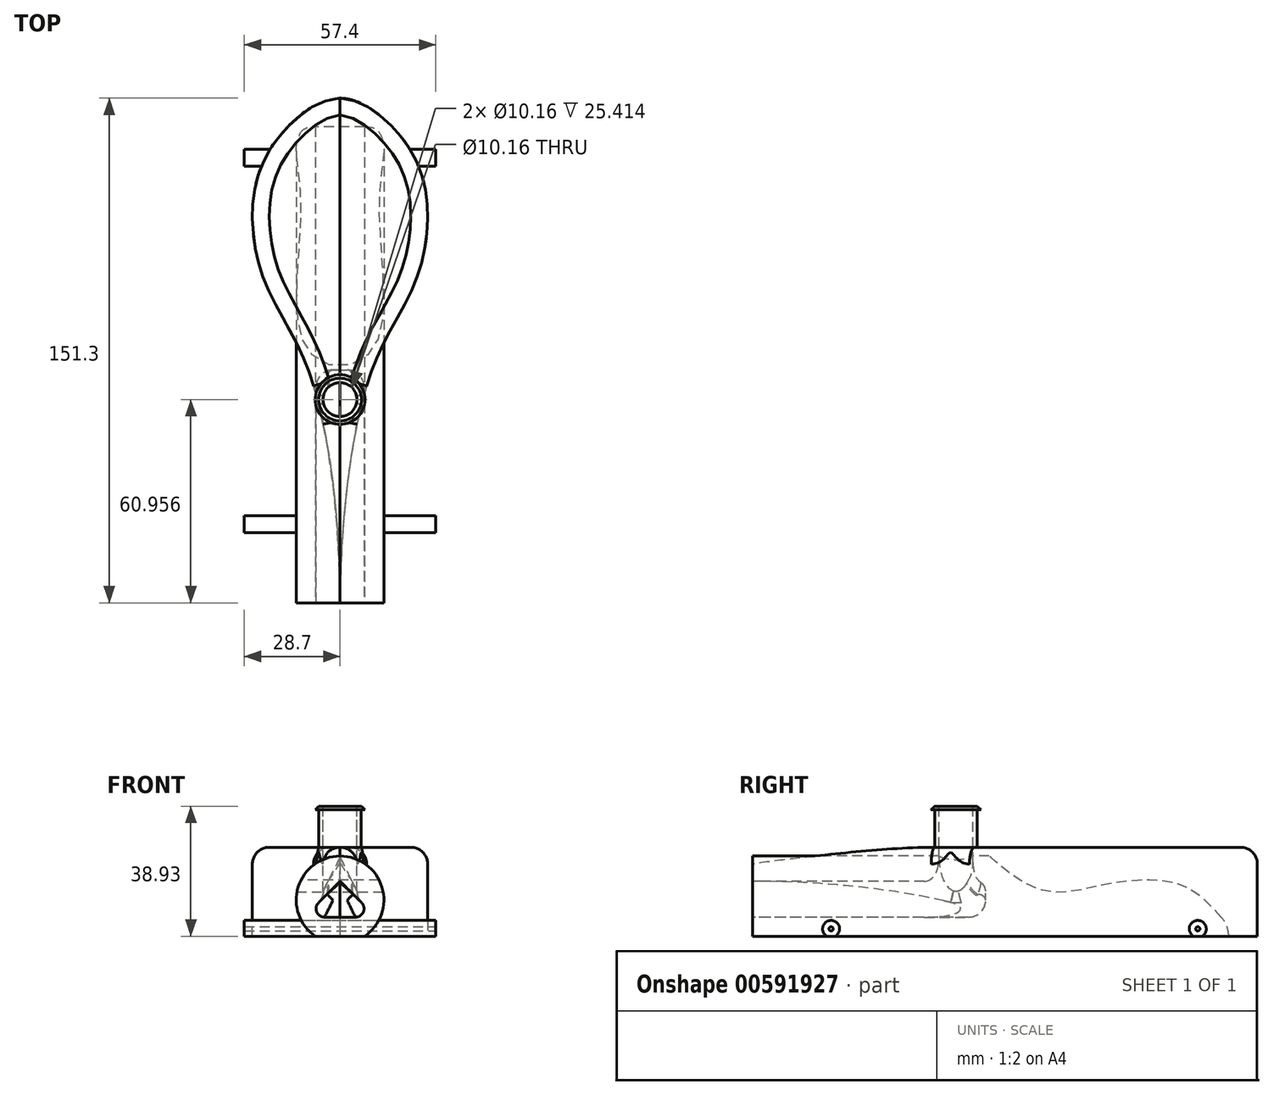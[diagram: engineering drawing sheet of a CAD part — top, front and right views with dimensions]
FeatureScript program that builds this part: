
annotation { "Feature Type Name" : "Feature", "Feature Type Description" : "" }
export const myFeature = defineFeature(function(context is Context, id is Id, definition is map)
    precondition{}
    {
        {
            var Q0;
            Q0=qCreatedBy(makeId("Right.planeOp"),FACE);
            var sketch = newSketch(context, id + "F0", { "sketchPlane" : qUnion([Q0])});
            skArc(sketch, "E0", {"start": v(34.57, 0) * mm, "mid": v(34, 3.03) * mm, "end": v(32.38, 5.66) * mm});
            skFitSpline(sketch, "E1", {"points": [v(32.38, 5.66) * mm, v(19.77, 15.55) * mm, v(-2.69, 15.42) * mm, v(-20.2, 13.5) * mm, v(-35.12, 22.16) * mm, v(-47.01, 29.03) * mm, v(-87.12, 25.6) * mm, v(-108.15, 26.13) * mm], "startDerivative": vector(-87.5, 96.16) * mm, "endDerivative": vector(-171.6, 17.01) * mm});
            skLineSegment(sketch, "E2", {"start": v(-108.15, 26.13) * mm, "end": v(-108.15, 0) * mm});
            skLineSegment(sketch, "E3", {"start": v(-108.15, 0) * mm, "end": v(34.57, 0) * mm});
            skSolve(sketch);
        }
        {
            var Q0;
            Q0=qSketchRegion(id+"F0",true);
            extrude(context, id + "F1", {"entities" : qUnion([Q0]), "endBound" : BoundingType.SYMMETRIC, "depth" : 50.8 * mm, "offsetDistance" : 25.4 * mm});
        }
        {
            var Q0;
            Q0=makeQuery(id+"F1.opExtrude","SWEPT_FACE",FACE,{"disambiguationData":[OSD([sQuery(id+"F0.wireOp",EDGE,"E2")])]});
            var sketch = newSketch(context, id + "F2", { "sketchPlane" : qUnion([Q0])});
            skCircle(sketch, "E4", {"center": v(0, 10.88) * mm, "radius": 13.14 * mm});
            skCircle(sketch, "E5", {"center": v(0, 10.88) * mm, "radius": 42.96 * mm});
            skSolve(sketch);
        }
        {
            var Q0;
            Q0 = qSketchRegion(id + "F2", true);
            extrude(context, id + "F3", {"entities" : qUnion([Q0]), "operationType" : NewBodyOperationType.REMOVE, "oppositeDirection" : true, "depth" : 175 * mm, "offsetDistance" : 25.4 * mm});
        }
        {
            var Q0;
            Q0=qCreatedBy(makeId("Top.planeOp"),FACE);
            var sketch = newSketch(context, id + "F4", { "sketchPlane" : qUnion([Q0])});
            skLineSegment(sketch, "E6", {"start": v(0, 43.15) * mm, "end": v(0, 43.15) * mm});
            skFitSpline(sketch, "E7", {"points": [v(0, 43.15) * mm, v(-11.67, 38.2) * mm, v(-24.8, 19.18) * mm, v(-22.86, -11.1) * mm, v(-9.97, -37.24) * mm, v(0, -108) * mm], "startDerivative": vector(-88.12, 0) * mm, "endDerivative": vector(1.08, -257.24) * mm});
            skLineSegment(sketch, "E8", {"start": v(0, -108) * mm, "end": v(0, 43.15) * mm});
            skSolve(sketch);
        }
        {
            var Q0;
            Q0 = qSketchRegion(id + "F4", true);
            extrude(context, id + "F5", {"entities" : qUnion([Q0]), "depth" : 26.67 * mm, "offsetDistance" : 25.4 * mm});
        }
        {
            var Q0;
            Q0=qCreatedBy(makeId("Right.planeOp"),FACE);
            var sketch = newSketch(context, id + "F6", { "sketchPlane" : qUnion([Q0])});
            skLineSegment(sketch, "E9", {"start": v(-47.2, 26.67) * mm, "end": v(-40.84, 26.67) * mm});
            skLineSegment(sketch, "E10", {"start": v(-40.84, 26.67) * mm, "end": v(-40.84, 37.94) * mm});
            skLineSegment(sketch, "E11", {"start": v(-40.84, 37.94) * mm, "end": v(-39.74, 37.94) * mm});
            skLineSegment(sketch, "E12", {"start": v(-39.74, 37.94) * mm, "end": v(-40.78, 38.93) * mm});
            skLineSegment(sketch, "E13", {"start": v(-40.78, 38.93) * mm, "end": v(-47.2, 38.93) * mm});
            skLineSegment(sketch, "E14", {"start": v(-47.2, 38.93) * mm, "end": v(-47.2, 26.67) * mm});
            skSolve(sketch);
        }
        {
            var Q0;
            Q0=qSketchRegion(id+"F6",true);
            var Q1;
            Q1=sQuery(id+"F6.wireOp",EDGE,"E14");
            revolve(context, id + "F7", {"operationType" : NewBodyOperationType.ADD, "entities" : qUnion([Q0]), "axis" : qUnion([Q1]), "revolveType" : RevolveType.FULL});
        }
        {
            var Q0;
            Q0=makeQuery(id+"F7.opRevolve","SWEPT_FACE",FACE,{"disambiguationData":[OSD([sQuery(id+"F6.wireOp",EDGE,"E13")])]});
            var sketch = newSketch(context, id + "F8", { "sketchPlane" : qUnion([Q0])});
            skCircle(sketch, "E15", {"center": v(0, -47.2) * mm, "radius": 5.08 * mm});
            skSolve(sketch);
        }
        {
            var Q0;
            Q0=qSketchRegion(id+"F8",true);
            extrude(context, id + "F9", {"entities" : qUnion([Q0]), "operationType" : NewBodyOperationType.REMOVE, "oppositeDirection" : true, "depth" : 32.77 * mm, "offsetDistance" : 25.4 * mm});
        }
        {
            var Q0;
            Q0=makeQuery(id+"F1.opExtrude","SWEPT_FACE",FACE,{"disambiguationData":[OSD([sQuery(id+"F0.wireOp",EDGE,"E2")])]});
            var sketch = newSketch(context, id + "F10", { "sketchPlane" : qUnion([Q0])});
            skLineSegment(sketch, "E16", {"start": v(0, 16.5) * mm, "end": v(-10.78, 5.71) * mm});
            skLineSegment(sketch, "E17", {"start": v(-10.78, 5.71) * mm, "end": v(0, 5.71) * mm});
            skLineSegment(sketch, "E18", {"start": v(0, 16.5) * mm, "end": v(10.78, 5.71) * mm});
            skLineSegment(sketch, "E19", {"start": v(10.78, 5.71) * mm, "end": v(0, 5.71) * mm});
            skSolve(sketch);
        }
        {
            var Q0;
            Q0=qSketchRegion(id+"F10",true);
            extrude(context, id + "F11", {"entities" : qUnion([Q0]), "operationType" : NewBodyOperationType.REMOVE, "endBound" : BoundingType.SYMMETRIC, "oppositeDirection" : true, "depth" : 139.7 * mm, "offsetDistance" : 25.4 * mm});
        }
        {
            var Q0;
            Q0=qCreatedBy(makeId("Right.planeOp"),FACE);
            var sketch = newSketch(context, id + "F12", { "sketchPlane" : qUnion([Q0])});
            skArc(sketch, "E20", {"start": v(-83.35, 0) * mm, "mid": v(-84.62, 4.74) * mm, "end": v(-85.89, 0) * mm});
            skCircle(sketch, "E21", {"center": v(-84.62, 2.2) * mm, "radius": 0.64 * mm});
            skLineSegment(sketch, "E22", {"start": v(-83.35, 0) * mm, "end": v(-85.89, 0) * mm});
            skArc(sketch, "E23", {"start": v(26.57, 0) * mm, "mid": v(25.3, 4.74) * mm, "end": v(24.03, 0) * mm});
            skCircle(sketch, "E24", {"center": v(25.3, 2.2) * mm, "radius": 0.64 * mm});
            skLineSegment(sketch, "E25", {"start": v(26.57, 0) * mm, "end": v(24.03, 0) * mm});
            skSolve(sketch);
        }
        {
            var Q0;
            Q0 = qSketchRegion(id + "F12", true);
            extrude(context, id + "F13", {"entities" : qUnion([Q0]), "endBound" : BoundingType.SYMMETRIC, "oppositeDirection" : true, "depth" : 57.4 * mm, "offsetDistance" : 25.4 * mm});
        }
        {
            var Q0;
            Q0=makeQuery(id+"F11.boolean.opBoolean","COPY",EDGE,{"derivedFrom":makeQuery(id+"F11.opExtrude","CAP_EDGE",EDGE,{"disambiguationData":[OSD([sQuery(id+"F10.wireOp",EDGE,"E17"),sQuery(id+"F10.wireOp",EDGE,"E19")])],"isStart":false})});
            fillet(context, id + "F14", {"entities" : qUnion([Q0]), "radius" : 5.08 * mm, "tangentPropagation" : true, "allowEdgeOverflow" : false});
        }
        {
            var Q0;
            Q0=makeQuery(id+"F11.boolean.opBoolean","COPY",EDGE,{"derivedFrom":makeQuery(id+"F11.opExtrude","CAP_EDGE",EDGE,{"disambiguationData":[OSD([sQuery(id+"F10.wireOp",EDGE,"E16")])],"isStart":false})});
            var Q1;
            Q1=makeQuery(id+"F11.boolean.opBoolean","COPY",EDGE,{"derivedFrom":makeQuery(id+"F11.opExtrude","CAP_EDGE",EDGE,{"disambiguationData":[OSD([sQuery(id+"F10.wireOp",EDGE,"E18")])],"isStart":false})});
            fillet(context, id + "F15", {"entities" : qUnion([Q0, Q1]), "radius" : 2.54 * mm, "tangentPropagation" : true, "allowEdgeOverflow" : false});
        }
        {
            var Q0;
            Q0=makeQuery(id+"F11.boolean.opBoolean","INTERSECT",EDGE,{"derivedFrom":[makeQuery(id+"F9.boolean.opBoolean","COPY",FACE,{"derivedFrom":makeQuery(id+"F9.opExtrude","SWEPT_FACE",FACE,{"disambiguationData":[OSD([sQuery(id+"F8.wireOp",EDGE,"E15")])]})}),makeQuery(id+"F11.opExtrude","SWEPT_FACE",FACE,{"disambiguationData":[OSD([sQuery(id+"F10.wireOp",EDGE,"E16")])]})]});
            var Q1;
            Q1=makeQuery(id+"F11.boolean.opBoolean","INTERSECT",EDGE,{"derivedFrom":[makeQuery(id+"F9.boolean.opBoolean","COPY",FACE,{"derivedFrom":makeQuery(id+"F9.opExtrude","SWEPT_FACE",FACE,{"disambiguationData":[OSD([sQuery(id+"F8.wireOp",EDGE,"E15")])]})}),makeQuery(id+"F11.opExtrude","SWEPT_FACE",FACE,{"disambiguationData":[OSD([sQuery(id+"F10.wireOp",EDGE,"E18")])]})]});
            fillet(context, id + "F16", {"entities" : qUnion([Q0, Q1]), "radius" : 5.08 * mm, "tangentPropagation" : true, "allowEdgeOverflow" : false});
        }
        {
            var Q0;
            Q0=makeQuery(id+"F5.opExtrude","SWEPT_BODY",BODY,{"disambiguationData":[OSD([sQuery(id+"F4.wireOp",EDGE,"E7"),sQuery(id+"F4.wireOp",EDGE,"E8")])]});
            var Q1;
            Q1=makeQuery(id+"F5.opExtrude","SWEPT_FACE",FACE,{"disambiguationData":[OSD([sQuery(id+"F4.wireOp",EDGE,"E8")])]});
            mirror(context, id + "F17", {"entities" : qUnion([Q0]), "mirrorPlane" : qUnion([Q1])});
        }
        {
            var Q0;
            Q0=makeQuery(id+"F5.opExtrude","CAP_EDGE",EDGE,{"disambiguationData":[OSD([sQuery(id+"F4.wireOp",EDGE,"E7")])],"isStart":false});
            var Q1;
            Q1=makeQuery(id+"F17.opPattern","COPY",EDGE,{"derivedFrom":makeQuery(id+"F5.opExtrude","CAP_EDGE",EDGE,{"disambiguationData":[OSD([sQuery(id+"F4.wireOp",EDGE,"E7")])],"isStart":false}),"instanceName":"1"});
            fillet(context, id + "F18", {"entities" : qUnion([Q0, Q1]), "radius" : 5.08 * mm, "tangentPropagation" : true, "allowEdgeOverflow" : false});
        }
    });
